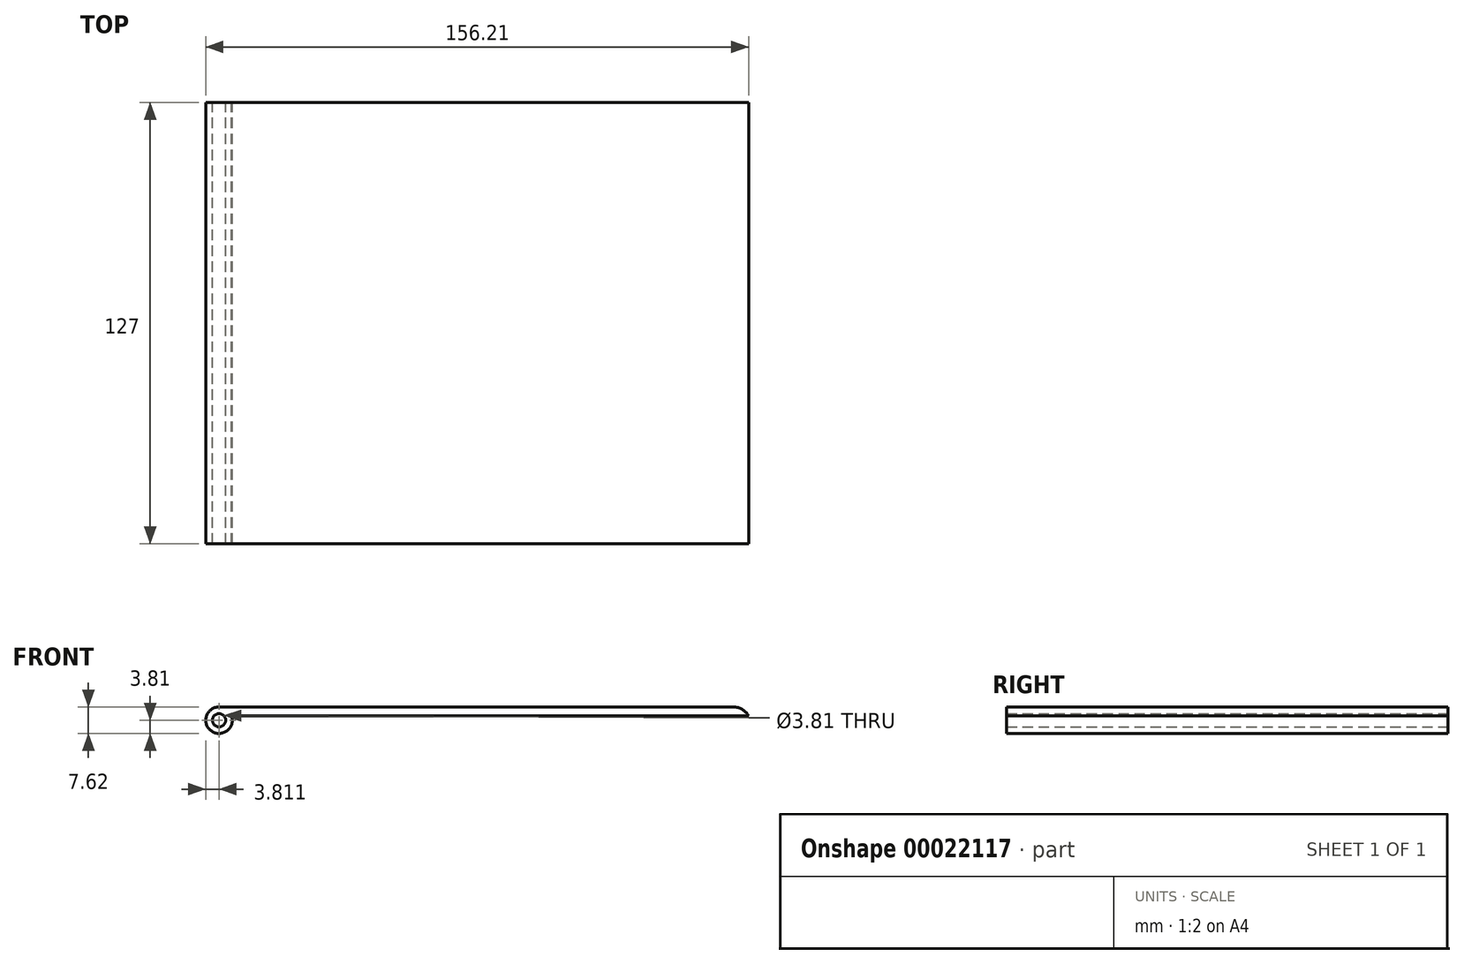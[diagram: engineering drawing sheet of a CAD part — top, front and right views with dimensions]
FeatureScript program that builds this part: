
annotation { "Feature Type Name" : "Feature", "Feature Type Description" : "" }
export const myFeature = defineFeature(function(context is Context, id is Id, definition is map)
    precondition{}
    {
        {
            var Q0;
            Q0=qCreatedBy(makeId("Front.planeOp"),FACE);
            var sketch = newSketch(context, id + "F0", { "sketchPlane" : qUnion([Q0])});
            skLineSegment(sketch, "E0.bottom", {"start": v(-12.2, 2.54) * mm, "end": v(140.2, 2.54) * mm});
            skLineSegment(sketch, "E0.top", {"start": v(-8.62, 0) * mm, "end": v(140.2, 0) * mm});
            skLineSegment(sketch, "E0.right", {"start": v(140.2, 2.54) * mm, "end": v(140.2, 0) * mm});
            skLineSegment(sketch, "E1", {"start": v(-12.2, 2.54) * mm, "end": v(-12.2, 2.54) * mm});
            skArc(sketch, "E2", {"start": v(-12.2, 2.54) * mm, "mid": v(-14.4, -4.38) * mm, "end": v(-8.62, 0) * mm});
            skLineSegment(sketch, "E3", {"start": v(-8.62, 0) * mm, "end": v(-12.2, -1.27) * mm});
            skCircle(sketch, "E4", {"center": v(-12.2, -1.27) * mm, "radius": 1.9 * mm});
            skSolve(sketch);
        }
        {
            var Q0;
            Q0=makeQuery(id+"F0.imprint","IMPRINT",FACE,{"disambiguationData":[TD([[makeQuery(id+"F0.imprint","IMPRINT",EDGE,{"derivedFrom":sQuery(id+"F0.wireOp",EDGE,"E0.bottom")}),-1.0]])]});
            extrude(context, id + "F1", {"entities" : qUnion([Q0]), "depth" : 127 * mm});
        }
        {
            var Q0;
            Q0=makeQuery(id+"F1.opExtrude","SWEPT_EDGE",EDGE,{"disambiguationData":[OSD([sQuery(id+"F0.wireOp",EDGE,"E0.bottom"),sQuery(id+"F0.wireOp",EDGE,"E0.right")])]});
            fillet(context, id + "F2", {"entities" : qUnion([Q0]), "radius" : 5.08 * mm, "tangentPropagation" : true, "allowEdgeOverflow" : false});
        }
    });
